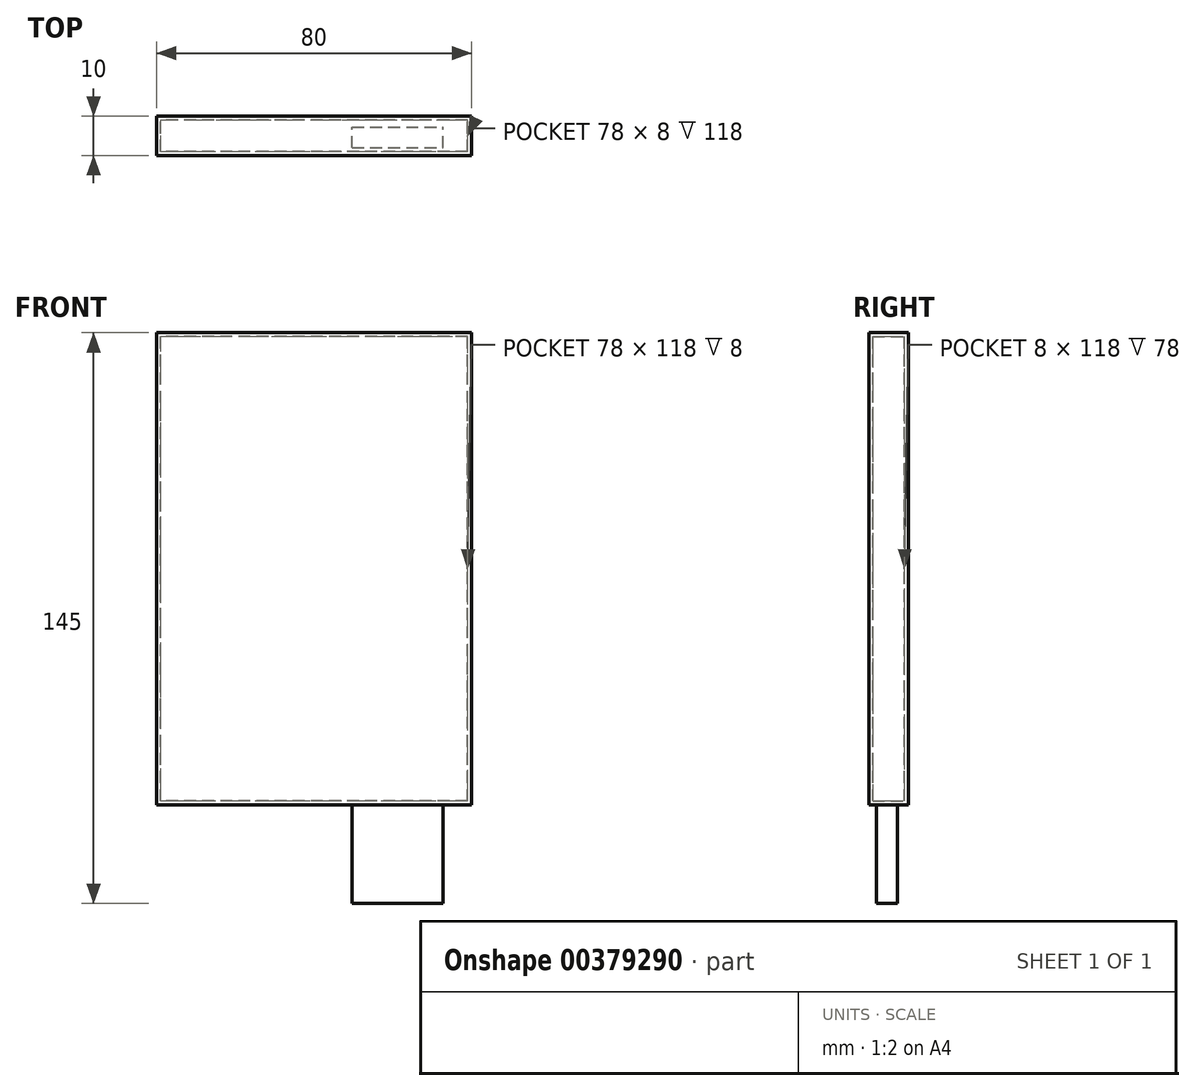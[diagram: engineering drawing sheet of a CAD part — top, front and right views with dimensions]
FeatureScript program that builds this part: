
annotation { "Feature Type Name" : "Feature", "Feature Type Description" : "" }
export const myFeature = defineFeature(function(context is Context, id is Id, definition is map)
    precondition{}
    {
        {
            var Q0;
            Q0=qCreatedBy(makeId("Front.planeOp"),FACE);
            var sketch = newSketch(context, id + "F0", { "sketchPlane" : qUnion([Q0])});
            skLineSegment(sketch, "E0.bottom", {"start": v(40, -60) * mm, "end": v(-40, -60) * mm});
            skLineSegment(sketch, "E0.top", {"start": v(40, 60) * mm, "end": v(-40, 60) * mm});
            skLineSegment(sketch, "E0.left", {"start": v(40, -60) * mm, "end": v(40, 60) * mm});
            skLineSegment(sketch, "E0.right", {"start": v(-40, -60) * mm, "end": v(-40, 60) * mm});
            skPoint(sketch, "E0.middle", {"position": v(0, 0) * mm});
            skSolve(sketch);
        }
        {
            var Q0;
            Q0=makeQuery(id+"F0.imprint","IMPRINT",FACE,{"disambiguationData":[TD([[makeQuery(id+"F0.imprint","IMPRINT",EDGE,{"derivedFrom":sQuery(id+"F0.wireOp",EDGE,"E0.bottom")}),-1.0]])]});
            extrude(context, id + "F1", {"entities" : qUnion([Q0]), "endBound" : BoundingType.SYMMETRIC, "depth" : 10 * mm});
        }
        {
            var Q0;
            Q0=makeQuery(id+"F1.opExtrude","CAP_FACE",FACE,{"disambiguationData":[OSD([sQuery(id+"F0.wireOp",EDGE,"E0.bottom"),sQuery(id+"F0.wireOp",EDGE,"E0.top"),sQuery(id+"F0.wireOp",EDGE,"E0.left"),sQuery(id+"F0.wireOp",EDGE,"E0.right")])],"isStart":false});
            var Q1;
            Q1=makeQuery(id+"F1.opExtrude","SWEPT_BODY",BODY,{"disambiguationData":[OSD([sQuery(id+"F0.wireOp",EDGE,"E0.bottom"),sQuery(id+"F0.wireOp",EDGE,"E0.top"),sQuery(id+"F0.wireOp",EDGE,"E0.left"),sQuery(id+"F0.wireOp",EDGE,"E0.right")])]});
            shell(context, id + "F2", {"isHollow" : true, "entities" : qUnion([Q0]), "parts" : qUnion([Q1]), "thickness" : 1 * mm});
        }
        {
            var Q0;
            Q0=makeQuery(id+"F1.opExtrude","SWEPT_FACE",FACE,{"disambiguationData":[OSD([sQuery(id+"F0.wireOp",EDGE,"E0.bottom")])]});
            var sketch = newSketch(context, id + "F3", { "sketchPlane" : qUnion([Q0])});
            skLineSegment(sketch, "E1.bottom", {"start": v(9.65, 3.03) * mm, "end": v(32.8, 3.03) * mm});
            skLineSegment(sketch, "E1.top", {"start": v(9.65, -2.22) * mm, "end": v(32.8, -2.22) * mm});
            skLineSegment(sketch, "E1.left", {"start": v(9.65, 3.03) * mm, "end": v(9.65, -2.22) * mm});
            skLineSegment(sketch, "E1.right", {"start": v(32.8, 3.03) * mm, "end": v(32.8, -2.22) * mm});
            skSolve(sketch);
        }
        {
            var Q0;
            Q0=makeQuery(id+"F3.imprint","IMPRINT",FACE,{"disambiguationData":[TD([[makeQuery(id+"F3.imprint","IMPRINT",EDGE,{"derivedFrom":sQuery(id+"F3.wireOp",EDGE,"E1.bottom")}),-1.0]])]});
            extrude(context, id + "F4", {"entities" : qUnion([Q0]), "operationType" : NewBodyOperationType.ADD, "depth" : 25 * mm});
        }
    });
